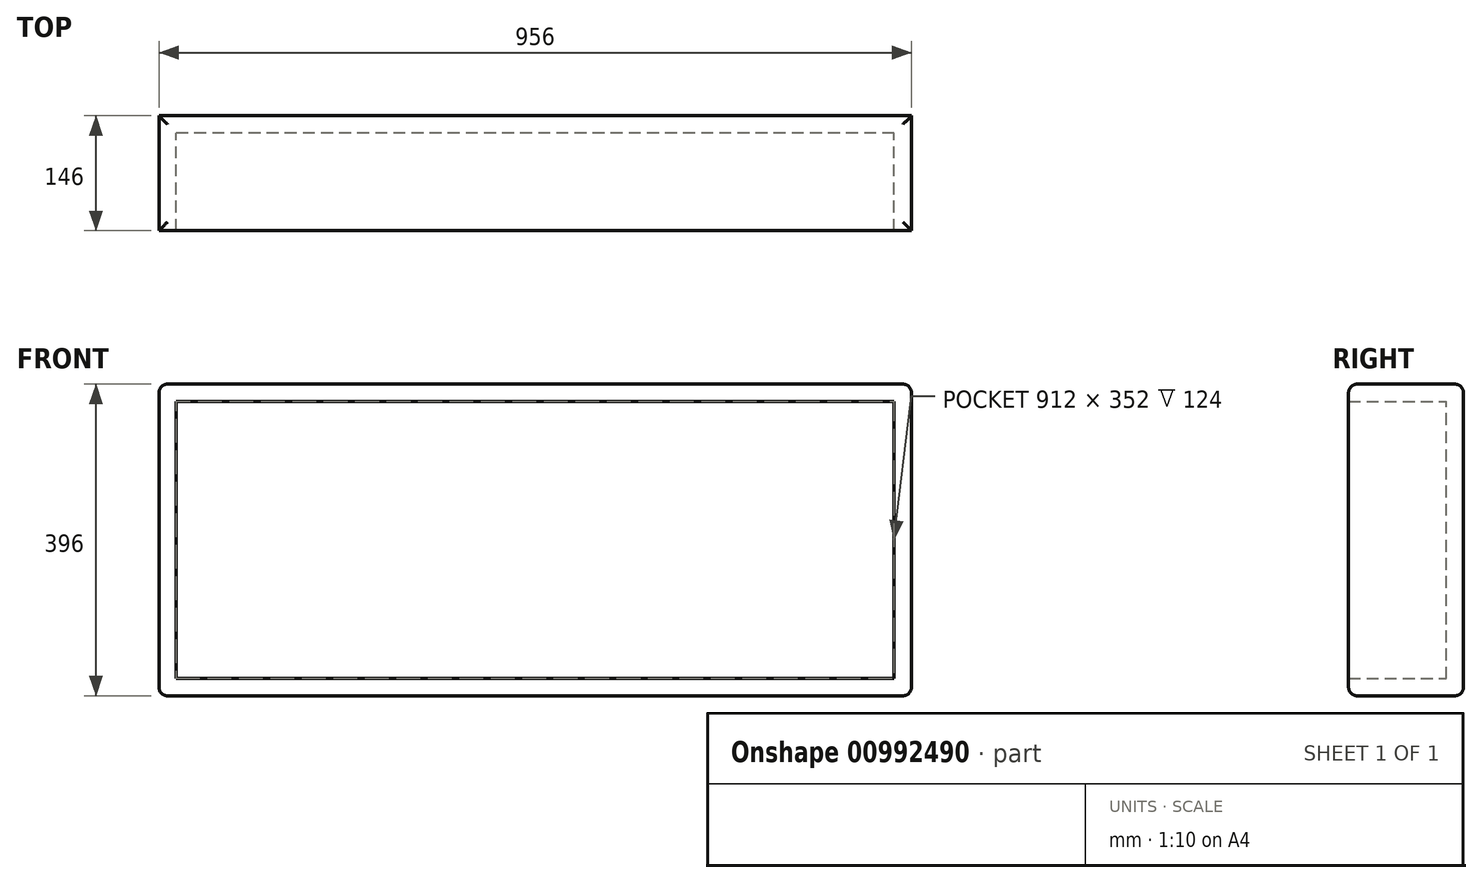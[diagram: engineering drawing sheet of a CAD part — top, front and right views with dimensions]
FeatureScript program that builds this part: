
annotation { "Feature Type Name" : "Feature", "Feature Type Description" : "" }
export const myFeature = defineFeature(function(context is Context, id is Id, definition is map)
    precondition{}
    {
        {
            var Q0;
            Q0=qCreatedBy(makeId("Front.planeOp"),FACE);
            var sketch = newSketch(context, id + "F0", { "sketchPlane" : qUnion([Q0])});
            skLineSegment(sketch, "E0.bottom", {"start": v(478, -198) * mm, "end": v(-478, -198) * mm});
            skLineSegment(sketch, "E0.top", {"start": v(478, 198) * mm, "end": v(-478, 198) * mm});
            skLineSegment(sketch, "E0.left", {"start": v(478, -198) * mm, "end": v(478, 198) * mm});
            skLineSegment(sketch, "E0.right", {"start": v(-478, -198) * mm, "end": v(-478, 198) * mm});
            skPoint(sketch, "E0.middle", {"position": v(0, 0) * mm});
            skSolve(sketch);
        }
        {
            var Q0;
            Q0=makeQuery(id+"F0.imprint","IMPRINT",FACE,{"disambiguationData":[TD([[makeQuery(id+"F0.imprint","IMPRINT",EDGE,{"derivedFrom":sQuery(id+"F0.wireOp",EDGE,"E0.bottom")}),-1.0]])]});
            extrude(context, id + "F1", {"entities" : qUnion([Q0]), "depth" : 146 * mm, "offsetDistance" : 25 * mm});
        }
        {
            var Q0;
            Q0=makeQuery(id+"F1.opExtrude","CAP_FACE",FACE,{"disambiguationData":[OSD([sQuery(id+"F0.wireOp",EDGE,"E0.bottom"),sQuery(id+"F0.wireOp",EDGE,"E0.top"),sQuery(id+"F0.wireOp",EDGE,"E0.left"),sQuery(id+"F0.wireOp",EDGE,"E0.right")])],"isStart":false});
            shell(context, id + "F2", {"entities" : qUnion([Q0]), "thickness" : 22 * mm});
        }
        {
            var Q0;
            Q0=makeQuery(id+"F1.opExtrude","SWEPT_FACE",FACE,{"disambiguationData":[OSD([sQuery(id+"F0.wireOp",EDGE,"E0.bottom")])]});
            fillet(context, id + "F3", {"entities" : qUnion([Q0]), "radius" : 11 * mm, "tangentPropagation" : true, "allowEdgeOverflow" : false});
        }
        {
            var Q0;
            Q0=makeQuery(id+"F1.opExtrude","SWEPT_FACE",FACE,{"disambiguationData":[OSD([sQuery(id+"F0.wireOp",EDGE,"E0.top")])]});
            fillet(context, id + "F4", {"entities" : qUnion([Q0]), "radius" : 11 * mm, "tangentPropagation" : true, "allowEdgeOverflow" : false});
        }
    });
